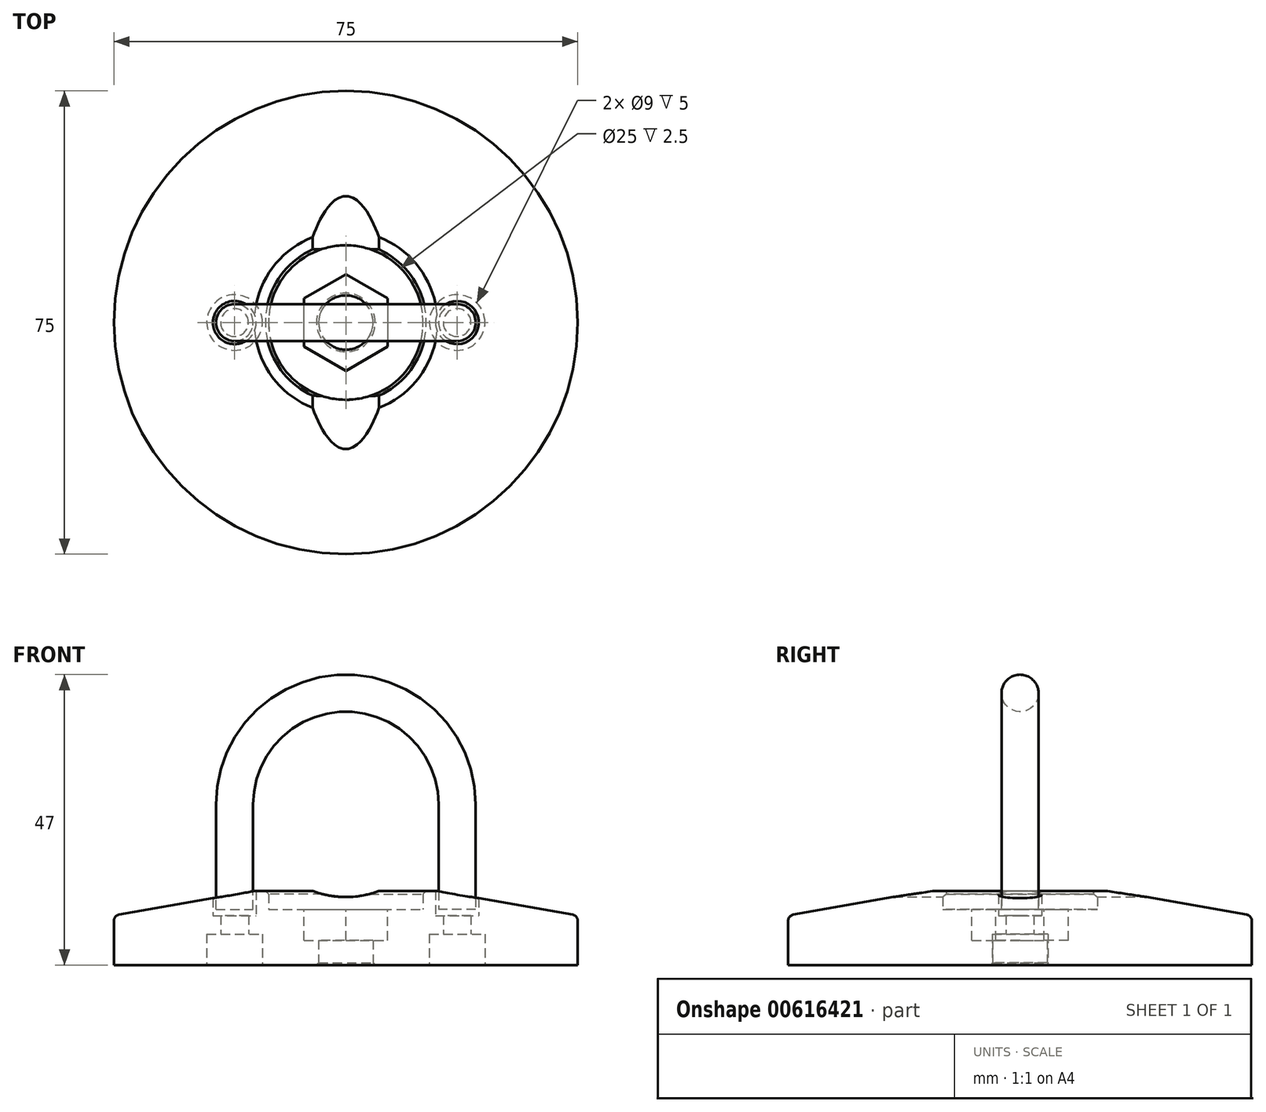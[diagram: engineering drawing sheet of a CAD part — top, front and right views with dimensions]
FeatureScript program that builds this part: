
annotation { "Feature Type Name" : "Feature", "Feature Type Description" : "" }
export const myFeature = defineFeature(function(context is Context, id is Id, definition is map)
    precondition{}
    {
        {
            var Q0;
            Q0=qCreatedBy(makeId("Front.planeOp"),FACE);
            var sketch = newSketch(context, id + "F0", { "sketchPlane" : qUnion([Q0])});
            skLineSegment(sketch, "E0", {"start": v(0, 0) * mm, "end": v(-37.5, 0) * mm});
            skLineSegment(sketch, "E1", {"start": v(-37.5, 0) * mm, "end": v(-37.5, 8) * mm});
            skLineSegment(sketch, "E2", {"start": v(-37.5, 8) * mm, "end": v(-14.81, 12) * mm});
            skLineSegment(sketch, "E3", {"start": v(0, 0) * mm, "end": v(0, 9) * mm, "construction": true});
            skLineSegment(sketch, "E4", {"start": v(0, 9) * mm, "end": v(0, 0) * mm});
            skLineSegment(sketch, "E5", {"start": v(-14.81, 12) * mm, "end": v(-12.5, 12) * mm});
            skLineSegment(sketch, "E6.trimOffspring", {"start": v(0, 14.61) * mm, "end": v(0, 29.03) * mm, "construction": true});
            skLineSegment(sketch, "E7", {"start": v(-12.5, 12) * mm, "end": v(-12.5, 9) * mm});
            skLineSegment(sketch, "E8", {"start": v(-12.5, 9) * mm, "end": v(0, 9) * mm});
            skPoint(sketch, "E9.orphan", {"position": v(0, 12) * mm});
            skSolve(sketch);
        }
        {
            var Q0;
            Q0=makeQuery(id+"F0.imprint","IMPRINT",FACE,{"disambiguationData":[TD([[makeQuery(id+"F0.imprint","IMPRINT",EDGE,{"derivedFrom":sQuery(id+"F0.wireOp",EDGE,"E0")}),-1.0]])]});
            var Q1;
            Q1=sQuery(id+"F0.wireOp",EDGE,"E6.trimOffspring");
            revolve(context, id + "F1", {"entities" : qUnion([Q0]), "axis" : qUnion([Q1]), "revolveType" : RevolveType.FULL});
        }
        {
            var Q0;
            Q0=makeQuery(id+"F1.opRevolve","SWEPT_EDGE",EDGE,{"disambiguationData":[OSD([sQuery(id+"F0.wireOp",EDGE,"E5"),sQuery(id+"F0.wireOp",EDGE,"E7")])]});
            chamfer(context, id + "F2", {"entities" : qUnion([Q0]), "width" : .5 * mm, "tangentPropagation" : true});
        }
        {
            var Q0;
            Q0=qCreatedBy(makeId("Front.planeOp"),FACE);
            var sketch = newSketch(context, id + "F3", { "sketchPlane" : qUnion([Q0])});
            skCircle(sketch, "E10", {"center": v(0, 26) * mm, "radius": 15 * mm});
            skPoint(sketch, "E11", {"position": v(0, 11) * mm});
            skSolve(sketch);
        }
        {
            var Q0;
            Q0 = qSketchRegion(id + "F3", true);
            extrude(context, id + "F4", {"entities" : qUnion([Q0]), "endBound" : BoundingType.SYMMETRIC, "depth" : 100 * mm, "offsetDistance" : 25 * mm});
        }
        {
            var Q0;
            Q0=makeQuery(id+"F4.opExtrude","SWEPT_BODY",BODY,{"disambiguationData":[OSD([sQuery(id+"F3.wireOp",EDGE,"E10")])]});
            var Q1;
            Q1=makeQuery(id+"FDrsC9OXBmPSGLZ_2.opPattern","COPY",BODY,{"derivedFrom":makeQuery(id+"F4.opExtrude","SWEPT_BODY",BODY,{"disambiguationData":[OSD([sQuery(id+"F3.wireOp",EDGE,"E10")])]}),"instanceName":"1"});
            var Q2;
            Q2=makeQuery(id+"F1.opRevolve","SWEPT_BODY",BODY,{"disambiguationData":[OSD([sQuery(id+"F0.wireOp",EDGE,"E0"),sQuery(id+"F0.wireOp",EDGE,"E1"),sQuery(id+"F0.wireOp",EDGE,"E2"),sQuery(id+"F0.wireOp",EDGE,"E4"),sQuery(id+"F0.wireOp",EDGE,"E5"),sQuery(id+"F0.wireOp",EDGE,"E7"),sQuery(id+"F0.wireOp",EDGE,"E8")])]});
            booleanBodies(context, id + "F5", {"operationType" : BooleanOperationType.SUBTRACTION, "tools" : qUnion([Q0, Q1]), "targets" : qUnion([Q2])});
        }
        {
            var Q0;
            Q0=qCreatedBy(makeId("Front.planeOp"),FACE);
            var sketch = newSketch(context, id + "F6", { "sketchPlane" : qUnion([Q0])});
            skArc(sketch, "E12", {"start": v(-18, 26) * mm, "mid": v(-12.73, 38.73) * mm, "end": v(0, 44) * mm});
            skLineSegment(sketch, "E13", {"start": v(-18, 26) * mm, "end": v(-18, 9) * mm});
            skArc(sketch, "E14.MirrorCS", {"start": v(18, 26) * mm, "mid": v(12.73, 38.73) * mm, "end": v(0, 44) * mm});
            skLineSegment(sketch, "E15.MirrorCS", {"start": v(18, 26) * mm, "end": v(18, 9) * mm});
            skSolve(sketch);
        }
        {
            var Q0;
            Q0=sQuery(id+"F6.wireOp",VERTEX,"E13.end");
            var Q1;
            Q1=sQuery(id+"F6.wireOp",EDGE,"E13");
            cPlane(context, id + "F7", {"entities" : qUnion([Q0, Q1]), "cplaneType" : CPlaneType.LINE_POINT, "offset" : 25 * mm, "width" : 150 * mm, "height" : 150 * mm});
        }
        {
            var Q0;
            Q0=qCreatedBy(id+"F7.planeOp",FACE);
            var sketch = newSketch(context, id + "F8", { "sketchPlane" : qUnion([Q0])});
            skPoint(sketch, "E16.0", {"position": v(-18, 0) * mm});
            skCircle(sketch, "E17", {"center": v(-18, 0) * mm, "radius": 3 * mm});
            skSolve(sketch);
        }
        {
            var Q0;
            Q0 = qSketchRegion(id + "F8", true);
            var Q1;
            Q1 = qConstructionFilter(qBodyType(qCreatedBy(id + "F6" ,EDGE), BodyType.WIRE), ConstructionObject.NO);
            sweep(context, id + "F9", {"profiles" : qUnion([Q0]), "path" : qUnion([Q1])});
        }
        {
            var Q0;
            Q0=makeQuery(id+"F9.opSweep","CAP_FACE",FACE,{"disambiguationData":[OSD([sQuery(id+"F6.wireOp",VERTEX,"E13.end"),sQuery(id+"F8.wireOp",EDGE,"E17")])],"isStart":true});
            cPlane(context, id + "F10", {"entities" : qUnion([Q0]), "cplaneType" : CPlaneType.OFFSET, "offset" : 1 * mm, "width" : 150 * mm, "height" : 150 * mm});
        }
        {
            var Q0;
            Q0=qCreatedBy(id+"F10.planeOp",FACE);
            var sketch = newSketch(context, id + "F11", { "sketchPlane" : qUnion([Q0])});
            skPoint(sketch, "E18", {"position": v(-18, 0) * mm});
            skPoint(sketch, "E19.MirrorP", {"position": v(18, 0) * mm});
            skSolve(sketch);
        }
        {
            var Q0;
            Q0=sQuery(id+"F11.wireOp",VERTEX,"E18");
            var Q1;
            Q1=sQuery(id+"F11.wireOp",VERTEX,"E19.MirrorP");
            var Q2;
            Q2=makeQuery(id+"F1.opRevolve","SWEPT_BODY",BODY,{"disambiguationData":[OSD([sQuery(id+"F0.wireOp",EDGE,"E0"),sQuery(id+"F0.wireOp",EDGE,"E1"),sQuery(id+"F0.wireOp",EDGE,"E2"),sQuery(id+"F0.wireOp",EDGE,"E4"),sQuery(id+"F0.wireOp",EDGE,"E5"),sQuery(id+"F0.wireOp",EDGE,"E7"),sQuery(id+"F0.wireOp",EDGE,"E8")])]});
            hole(context, id + "F12", {"style" : HoleStyle.SIMPLE, "endStyle" : HoleEndStyle.BLIND, "holeDiameter" : 7 * mm, "majorDiameter" : 5 * mm, "holeDepth" : 5.5 * mm, "isTappedThrough" : true, "tappedDepth" : 12 * mm, "tapClearance" : 3, "startFromSketch" : true, "locations" : qUnion([Q0, Q1]), "scope" : qUnion([Q2])});
        }
        {
            var Q0;
            Q0=makeQuery(id+"F1.opRevolve","SWEPT_FACE",FACE,{"disambiguationData":[OSD([sQuery(id+"F0.wireOp",EDGE,"E0")])]});
            var sketch = newSketch(context, id + "F13", { "sketchPlane" : qUnion([Q0])});
            skCircle(sketch, "E20.0.0", {"center": v(0, 0) * mm, "radius": 37.5 * mm});
            skPoint(sketch, "E21", {"position": v(-18, 0) * mm});
            skPoint(sketch, "E22.MirrorP", {"position": v(18, 0) * mm});
            skSolve(sketch);
        }
        {
            var Q0;
            Q0=sQuery(id+"F13.wireOp",VERTEX,"E21");
            var Q1;
            Q1=sQuery(id+"F13.wireOp",VERTEX,"E22.MirrorP");
            var Q2;
            Q2=makeQuery(id+"F1.opRevolve","SWEPT_BODY",BODY,{"disambiguationData":[OSD([sQuery(id+"F0.wireOp",EDGE,"E0"),sQuery(id+"F0.wireOp",EDGE,"E1"),sQuery(id+"F0.wireOp",EDGE,"E2"),sQuery(id+"F0.wireOp",EDGE,"E4"),sQuery(id+"F0.wireOp",EDGE,"E5"),sQuery(id+"F0.wireOp",EDGE,"E7"),sQuery(id+"F0.wireOp",EDGE,"E8")])]});
            hole(context, id + "F14", {"style" : HoleStyle.C_BORE, "endStyle" : HoleEndStyle.THROUGH, "holeDiameter" : 4.5 * mm, "cBoreDiameter" : 9 * mm, "cBoreDepth" : 5 * mm, "majorDiameter" : 5 * mm, "isTappedThrough" : true, "tappedDepth" : 12 * mm, "tapClearance" : 3, "startFromSketch" : true, "locations" : qUnion([Q0, Q1]), "scope" : qUnion([Q2])});
        }
        {
            var Q0;
            Q0=sQuery(id+"F13.wireOp",VERTEX,"E20.0.0.center");
            var Q1;
            Q1=makeQuery(id+"F1.opRevolve","SWEPT_BODY",BODY,{"disambiguationData":[OSD([sQuery(id+"F0.wireOp",EDGE,"E0"),sQuery(id+"F0.wireOp",EDGE,"E1"),sQuery(id+"F0.wireOp",EDGE,"E2"),sQuery(id+"F0.wireOp",EDGE,"E4"),sQuery(id+"F0.wireOp",EDGE,"E5"),sQuery(id+"F0.wireOp",EDGE,"E7"),sQuery(id+"F0.wireOp",EDGE,"E8")])]});
            hole(context, id + "F15", {"style" : HoleStyle.C_SINK, "endStyle" : HoleEndStyle.THROUGH, "holeDiameter" : 8.8 * mm, "cSinkDiameter" : 9.5 * mm, "cSinkAngle" : 90 * degree, "majorDiameter" : 5 * mm, "isTappedThrough" : true, "tappedDepth" : 12 * mm, "tapClearance" : 3, "startFromSketch" : true, "locations" : qUnion([Q0]), "scope" : qUnion([Q1])});
        }
        {
            var Q0;
            Q0=makeQuery(id+"F1.opRevolve","SWEPT_FACE",FACE,{"disambiguationData":[OSD([sQuery(id+"F0.wireOp",EDGE,"E8")])]});
            var sketch = newSketch(context, id + "F16", { "sketchPlane" : qUnion([Q0])});
            skCircle(sketch, "E23.cCircle", {"center": v(0, 0) * mm, "radius": 7.8 * mm, "construction": true});
            skLineSegment(sketch, "E23.0", {"start": v(0, 7.8) * mm, "end": v(6.75, 3.9) * mm});
            skLineSegment(sketch, "E23.1", {"start": v(6.75, 3.9) * mm, "end": v(6.75, -3.9) * mm});
            skLineSegment(sketch, "E23.2", {"start": v(6.75, -3.9) * mm, "end": v(0, -7.8) * mm});
            skLineSegment(sketch, "E23.3", {"start": v(0, -7.8) * mm, "end": v(-6.75, -3.9) * mm});
            skLineSegment(sketch, "E23.4", {"start": v(-6.75, -3.9) * mm, "end": v(-6.75, 3.9) * mm});
            skLineSegment(sketch, "E23.5", {"start": v(-6.75, 3.9) * mm, "end": v(0, 7.8) * mm});
            skSolve(sketch);
        }
        {
            var Q0;
            Q0 = qSketchRegion(id + "F16", true);
            extrude(context, id + "F17", {"entities" : qUnion([Q0]), "operationType" : NewBodyOperationType.REMOVE, "oppositeDirection" : true, "depth" : 5 * mm, "offsetDistance" : 25 * mm});
        }
        {
            var Q0;
            Q0=makeQuery(id+"F1.opRevolve","SWEPT_EDGE",EDGE,{"disambiguationData":[OSD([sQuery(id+"F0.wireOp",EDGE,"E1"),sQuery(id+"F0.wireOp",EDGE,"E2")])]});
            fillet(context, id + "F18", {"entities" : qUnion([Q0]), "radius" : 1 * mm, "tangentPropagation" : true, "allowEdgeOverflow" : false});
        }
    });
